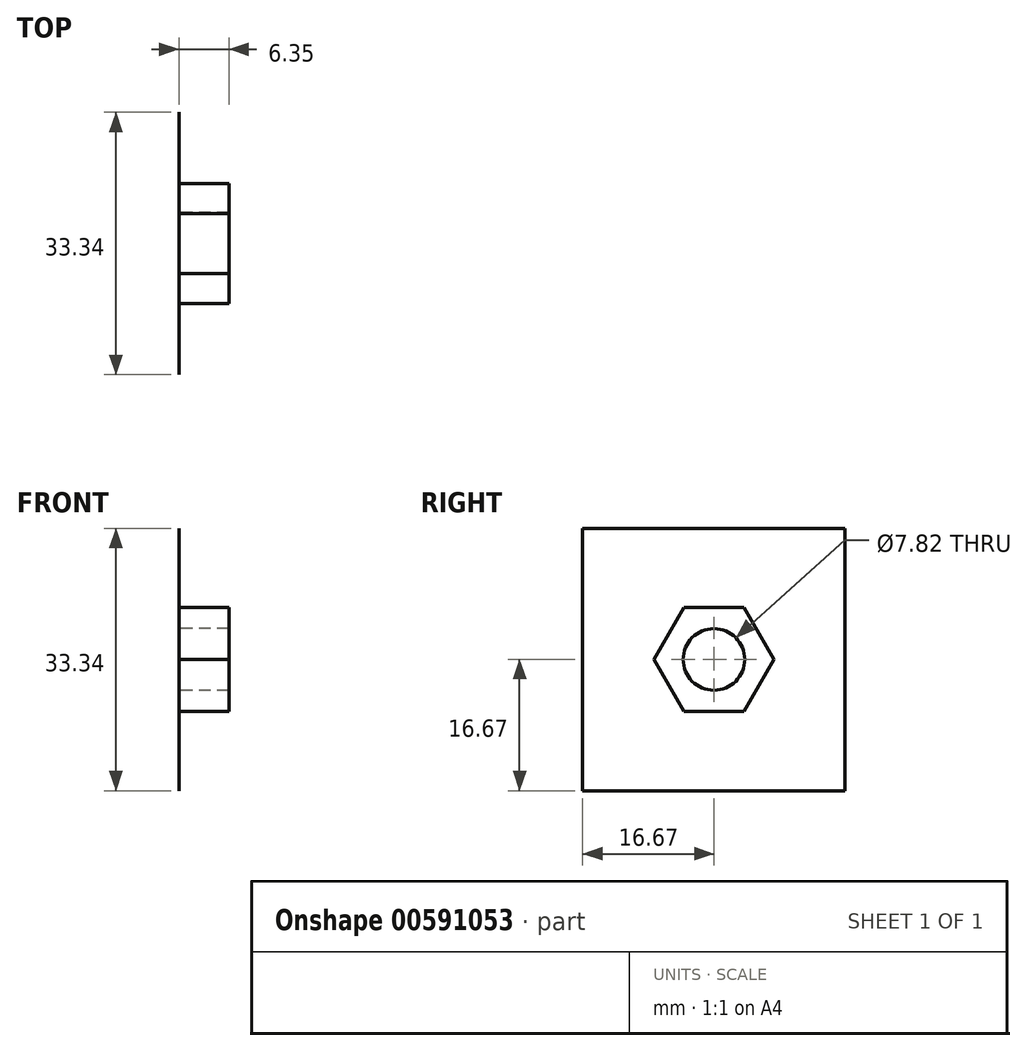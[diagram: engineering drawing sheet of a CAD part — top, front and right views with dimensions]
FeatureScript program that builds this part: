
annotation { "Feature Type Name" : "Feature", "Feature Type Description" : "" }
export const myFeature = defineFeature(function(context is Context, id is Id, definition is map)
    precondition{}
    {
        {
            var Q0;
            Q0=qCreatedBy(makeId("Right.planeOp"),FACE);
            var sketch = newSketch(context, id + "F0", { "sketchPlane" : qUnion([Q0])});
            skLineSegment(sketch, "E0.bottom", {"start": v(4.41, 5.56) * mm, "end": v(3.56, 5.56) * mm});
            skLineSegment(sketch, "E0.top", {"start": v(4.41, -5.56) * mm, "end": v(3.56, -5.56) * mm});
            skLineSegment(sketch, "E0.left", {"start": v(16.67, 5.56) * mm, "end": v(16.67, -5.56) * mm});
            skLineSegment(sketch, "E0.right", {"start": v(-16.67, 5.56) * mm, "end": v(-16.67, -5.56) * mm});
            skPoint(sketch, "E0.middle", {"position": v(0, 0) * mm});
            skLineSegment(sketch, "E1.MirrorCS", {"start": v(-16.67, -16.67) * mm, "end": v(-16.67, -5.56) * mm});
            skLineSegment(sketch, "E2.MirrorCS", {"start": v(16.67, -16.67) * mm, "end": v(-16.67, -16.67) * mm});
            skLineSegment(sketch, "E3.MirrorCS", {"start": v(16.67, -16.67) * mm, "end": v(16.67, -5.56) * mm});
            skLineSegment(sketch, "E4.MirrorCS", {"start": v(-16.67, 5.56) * mm, "end": v(-16.67, 16.67) * mm});
            skLineSegment(sketch, "E5.MirrorCS", {"start": v(16.67, 16.67) * mm, "end": v(-16.67, 16.67) * mm});
            skLineSegment(sketch, "E6.MirrorCS", {"start": v(16.67, 5.56) * mm, "end": v(16.67, 16.67) * mm});
            skLineSegment(sketch, "E7.bottom", {"start": v(16.67, 5.56) * mm, "end": v(46.83, 5.56) * mm});
            skLineSegment(sketch, "E7.top", {"start": v(16.67, -5.57) * mm, "end": v(46.83, -5.57) * mm});
            skLineSegment(sketch, "E7.left", {"start": v(16.67, 5.56) * mm, "end": v(16.67, -5.57) * mm});
            skLineSegment(sketch, "E7.right", {"start": v(46.83, 5.56) * mm, "end": v(46.83, -5.57) * mm});
            skLineSegment(sketch, "E8.bottom", {"start": v(-16.67, 5.56) * mm, "end": v(-46.84, 5.56) * mm});
            skLineSegment(sketch, "E8.top", {"start": v(-16.67, -5.57) * mm, "end": v(-46.84, -5.57) * mm});
            skLineSegment(sketch, "E8.left", {"start": v(-16.67, 5.56) * mm, "end": v(-16.67, -5.57) * mm});
            skLineSegment(sketch, "E8.right", {"start": v(-46.84, 5.56) * mm, "end": v(-46.84, -5.57) * mm});
            skCircle(sketch, "E9.cCircle", {"center": v(0, 0) * mm, "radius": 6.6 * mm, "construction": true});
            skPoint(sketch, "E9.cCircle.perimeterSnap0", {"position": v(0, 5.56) * mm});
            skLineSegment(sketch, "E9.0", {"start": v(-3.81, 6.6) * mm, "end": v(3.8, 6.6) * mm});
            skLineSegment(sketch, "E9.1", {"start": v(3.8, 6.6) * mm, "end": v(7.62, 0) * mm});
            skLineSegment(sketch, "E9.2", {"start": v(7.62, 0) * mm, "end": v(3.8, -6.6) * mm});
            skLineSegment(sketch, "E9.3", {"start": v(3.81, -6.6) * mm, "end": v(-3.8, -6.6) * mm});
            skLineSegment(sketch, "E9.4", {"start": v(-3.8, -6.6) * mm, "end": v(-7.62, 0) * mm});
            skLineSegment(sketch, "E9.5", {"start": v(-7.62, 0) * mm, "end": v(-3.8, 6.6) * mm});
            skPoint(sketch, "E9.0.midPoint", {"position": v(0, 6.6) * mm});
            skPoint(sketch, "E9.0.midPoint.positionSnap0", {"position": v(0, 5.56) * mm});
            skLineSegment(sketch, "E10.trimOffspring", {"start": v(-3.56, 5.56) * mm, "end": v(-4.41, 5.56) * mm});
            skLineSegment(sketch, "E11.trimOffspring", {"start": v(-3.56, -5.56) * mm, "end": v(-4.41, -5.56) * mm});
            skCircle(sketch, "E12", {"center": v(0, 0) * mm, "radius": 3.91 * mm});
            skSolve(sketch);
        }
        {
            var Q0;
            Q0=makeQuery(id+"F0.imprint","IMPRINT",FACE,{"disambiguationData":[TD([[makeQuery(id+"F0.imprint","IMPRINT",EDGE,{"derivedFrom":sQuery(id+"F0.wireOp",EDGE,"E1.MirrorCS")}),-1.0]])]});
            var Q1;
            Q1=makeQuery(id+"F0.imprint","IMPRINT",FACE,{"disambiguationData":[TD([[makeQuery(id+"F0.imprint","IMPRINT",EDGE,{"derivedFrom":sQuery(id+"F0.wireOp",EDGE,"E8.bottom")}),1.0]])]});
            var Q2;
            Q2=makeQuery(id+"F0.imprint","IMPRINT",FACE,{"disambiguationData":[TD([[makeQuery(id+"F0.imprint","IMPRINT",EDGE,{"derivedFrom":sQuery(id+"F0.wireOp",EDGE,"E7.bottom")}),-1.0]])]});
            extrude(context, id + "F1", {"entities" : qUnion([Q0, Q1, Q2]), "depth" : 1 / 50.8 * mm, "offsetDistance" : 25.4 * mm});
        }
        {
            var Q0;
            {var subQ1=sQuery(id+"F0.wireOp",EDGE,"E9.0");Q0=makeQuery(id+"F0.imprint","IMPRINT",FACE,{"disambiguationData":[TD([[makeQuery(id+"F0.imprint","IMPRINT",EDGE,{"derivedFrom":subQ1}),-1.0]])]});}
            extrude(context, id + "F2", {"entities" : qUnion([Q0]), "operationType" : NewBodyOperationType.ADD, "depth" : 6.35 * mm, "offsetDistance" : 25.4 * mm});
        }
        {
            var Q0;
            Q0=makeQuery(id+"F0.imprint","IMPRINT",FACE,{"disambiguationData":[TD([[makeQuery(id+"F0.imprint","IMPRINT",EDGE,{"derivedFrom":sQuery(id+"F0.wireOp",EDGE,"E8.bottom")}),1.0]])]});
            var Q1;
            Q1=makeQuery(id+"F0.imprint","IMPRINT",FACE,{"disambiguationData":[TD([[makeQuery(id+"F0.imprint","IMPRINT",EDGE,{"derivedFrom":sQuery(id+"F0.wireOp",EDGE,"E7.bottom")}),-1.0]])]});
            extrude(context, id + "F3", {"entities" : qUnion([Q0, Q1]), "operationType" : NewBodyOperationType.REMOVE, "depth" : 6.35 * mm, "offsetDistance" : 25.4 * mm});
        }
    });
